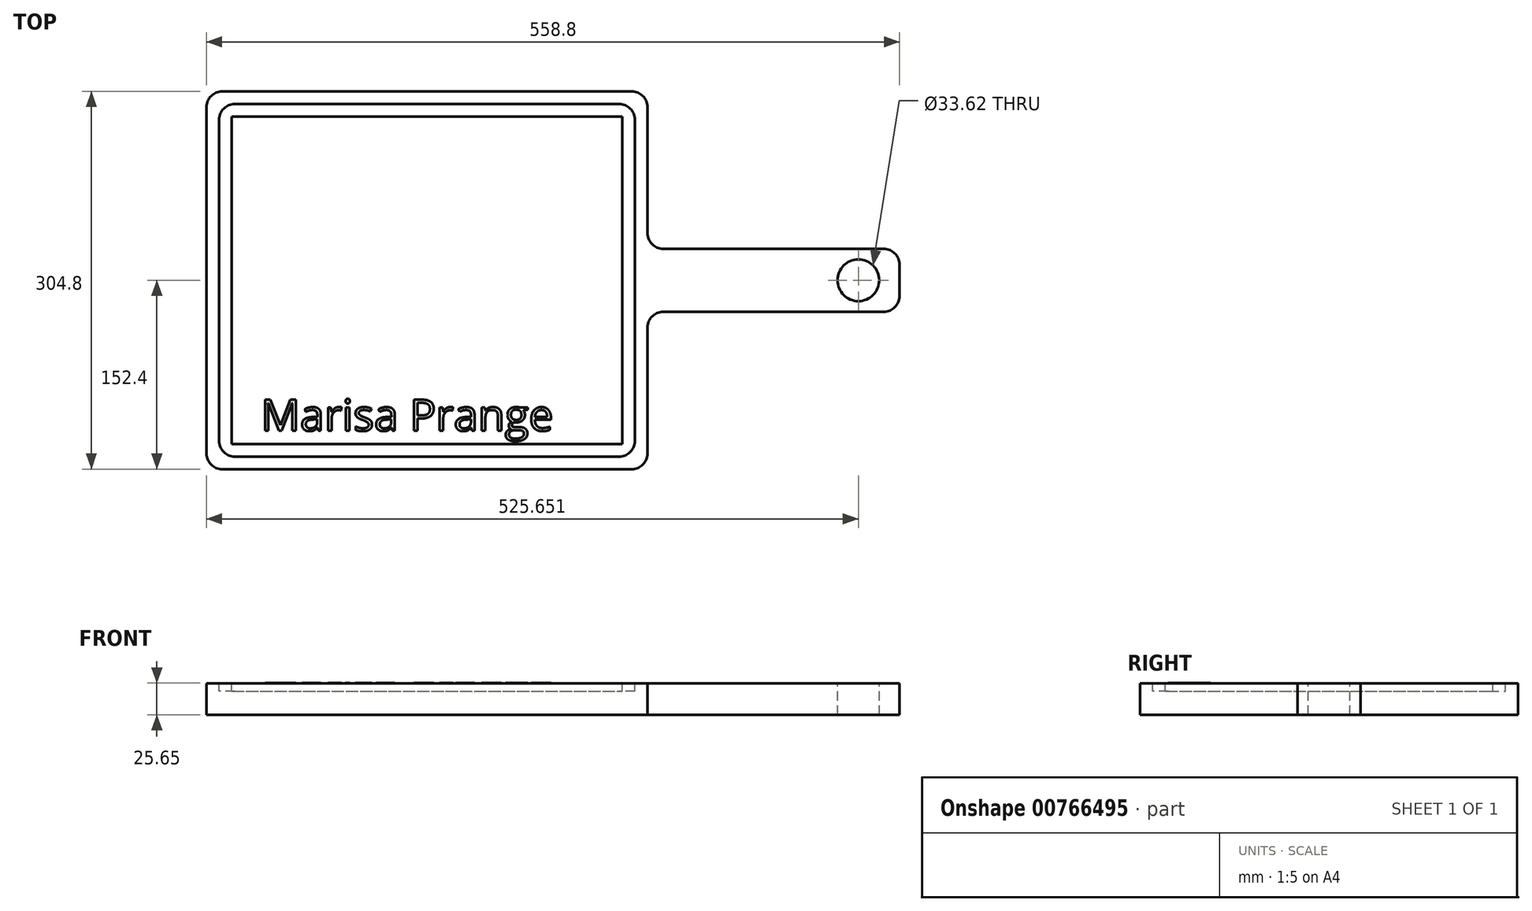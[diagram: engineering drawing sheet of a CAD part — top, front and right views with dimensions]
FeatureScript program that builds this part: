
annotation { "Feature Type Name" : "Feature", "Feature Type Description" : "" }
export const myFeature = defineFeature(function(context is Context, id is Id, definition is map)
    precondition{}
    {
        {
            var Q0;
            Q0=qCreatedBy(makeId("Top.planeOp"),FACE);
            var sketch = newSketch(context, id + "F0", { "sketchPlane" : qUnion([Q0])});
            skLineSegment(sketch, "E0.bottom", {"start": v(0, 0) * mm, "end": v(355.6, 0) * mm});
            skLineSegment(sketch, "E0.top", {"start": v(0, 304.8) * mm, "end": v(355.6, 304.8) * mm});
            skLineSegment(sketch, "E0.left", {"start": v(0, 0) * mm, "end": v(0, 304.8) * mm});
            skLineSegment(sketch, "E0.right", {"start": v(355.6, 0) * mm, "end": v(355.6, 304.8) * mm});
            skLineSegment(sketch, "E1.bottom", {"start": v(355.6, 177.8) * mm, "end": v(558.8, 177.8) * mm});
            skLineSegment(sketch, "E1.top", {"start": v(355.6, 127) * mm, "end": v(558.8, 127) * mm});
            skLineSegment(sketch, "E1.left", {"start": v(355.6, 177.8) * mm, "end": v(355.6, 127) * mm});
            skLineSegment(sketch, "E1.right", {"start": v(558.8, 177.8) * mm, "end": v(558.8, 127) * mm});
            skSolve(sketch);
        }
        {
            var Q0;
            {var subQ1=sQuery(id+"F0.wireOp",EDGE,"E0.bottom");Q0=makeQuery(id+"F0.imprint","IMPRINT",FACE,{"disambiguationData":[TD([[makeQuery(id+"F0.imprint","IMPRINT",EDGE,{"derivedFrom":subQ1}),1.0]])]});}
            var Q1;
            Q1=makeQuery(id+"F0.imprint","IMPRINT",FACE,{"disambiguationData":[TD([[makeQuery(id+"F0.imprint","IMPRINT",EDGE,{"derivedFrom":sQuery(id+"F0.wireOp",EDGE,"E1.bottom")}),-1.0]])]});
            extrude(context, id + "F1", {"entities" : qUnion([Q0, Q1]), "depth" : 25.4 * mm, "offsetDistance" : 25.4 * mm});
        }
        {
            var Q0;
            Q0=makeQuery(id+"F1.opExtrude","CAP_FACE",FACE,{"disambiguationData":[OSD([sQuery(id+"F0.wireOp",EDGE,"E0.bottom"),sQuery(id+"F0.wireOp",EDGE,"E0.top"),sQuery(id+"F0.wireOp",EDGE,"E0.left"),sQuery(id+"F0.wireOp",EDGE,"E0.right"),sQuery(id+"F0.wireOp",EDGE,"E1.bottom"),sQuery(id+"F0.wireOp",EDGE,"E1.top"),sQuery(id+"F0.wireOp",EDGE,"E1.right")])],"isStart":false});
            var sketch = newSketch(context, id + "F2", { "sketchPlane" : qUnion([Q0])});
            skCircle(sketch, "E2", {"center": v(525.65, 152.4) * mm, "radius": 16.81 * mm});
            skPoint(sketch, "E2.centerSnap0", {"position": v(558.8, 152.4) * mm});
            skSolve(sketch);
        }
        {
            var Q0;
            Q0 = qSketchRegion(id + "F2", true);
            extrude(context, id + "F3", {"entities" : qUnion([Q0]), "operationType" : NewBodyOperationType.REMOVE, "oppositeDirection" : true, "depth" : 25.4 * mm, "offsetDistance" : 25.4 * mm});
        }
        {
            var Q0;
            Q0=makeQuery(id+"F1.opExtrude","CAP_FACE",FACE,{"disambiguationData":[OSD([sQuery(id+"F0.wireOp",EDGE,"E0.bottom"),sQuery(id+"F0.wireOp",EDGE,"E0.top"),sQuery(id+"F0.wireOp",EDGE,"E0.left"),sQuery(id+"F0.wireOp",EDGE,"E0.right"),sQuery(id+"F0.wireOp",EDGE,"E1.bottom"),sQuery(id+"F0.wireOp",EDGE,"E1.top"),sQuery(id+"F0.wireOp",EDGE,"E1.right")])],"isStart":false});
            var sketch = newSketch(context, id + "F4", { "sketchPlane" : qUnion([Q0])});
            skLineSegment(sketch, "E3.0", {"start": v(345.44, 177.8) * mm, "end": v(345.44, 294.64) * mm});
            skLineSegment(sketch, "E3.1", {"start": v(345.44, 10.16) * mm, "end": v(345.44, 127) * mm});
            skLineSegment(sketch, "E3.2", {"start": v(10.16, 10.16) * mm, "end": v(345.44, 10.16) * mm});
            skLineSegment(sketch, "E3.3", {"start": v(10.16, 10.16) * mm, "end": v(10.16, 294.64) * mm});
            skLineSegment(sketch, "E3.4", {"start": v(10.16, 294.64) * mm, "end": v(345.44, 294.64) * mm});
            skLineSegment(sketch, "E4", {"start": v(345.44, 177.8) * mm, "end": v(345.44, 127) * mm});
            skLineSegment(sketch, "E5.0", {"start": v(20.32, 20.32) * mm, "end": v(20.32, 284.48) * mm});
            skLineSegment(sketch, "E5.1", {"start": v(335.28, 177.8) * mm, "end": v(335.28, 284.48) * mm});
            skLineSegment(sketch, "E5.2", {"start": v(335.28, 177.8) * mm, "end": v(335.28, 127) * mm});
            skLineSegment(sketch, "E5.3", {"start": v(20.32, 284.48) * mm, "end": v(335.28, 284.48) * mm});
            skLineSegment(sketch, "E5.4", {"start": v(335.28, 20.32) * mm, "end": v(335.28, 127) * mm});
            skLineSegment(sketch, "E5.5", {"start": v(20.32, 20.32) * mm, "end": v(335.28, 20.32) * mm});
            skText(sketch, "E6", { "text": "Marisa ", "fontName": "OpenSans-Regular.ttf"});
            const initialGuessF4  = {"E6": [0.02032, 0.0225, 1, 0, 0.0261]};
            skSetInitialGuess(sketch, initialGuessF4);
            skSolve(sketch);
        }
        {
            var Q0;
            Q0=makeQuery(id+"F4.imprint","IMPRINT",FACE,{"disambiguationData":[TD([[makeQuery(id+"F4.imprint","IMPRINT",EDGE,{"derivedFrom":sQuery(id+"F4.wireOp",EDGE,"E3.0")}),1.0]])]});
            extrude(context, id + "F5", {"entities" : qUnion([Q0]), "operationType" : NewBodyOperationType.REMOVE, "oppositeDirection" : true, "depth" : 6.35 * mm, "offsetDistance" : 25.4 * mm});
        }
        {
            var Q0;
            Q0=makeQuery(id+"F5.boolean.opBoolean","COPY",EDGE,{"derivedFrom":makeQuery(id+"F5.opExtrude","SWEPT_EDGE",EDGE,{"disambiguationData":[OSD([sQuery(id+"F4.wireOp",EDGE,"E3.3"),sQuery(id+"F4.wireOp",EDGE,"E3.4")])]})});
            var Q1;
            Q1=makeQuery(id+"F5.boolean.opBoolean","COPY",EDGE,{"derivedFrom":makeQuery(id+"F5.opExtrude","SWEPT_EDGE",EDGE,{"disambiguationData":[OSD([sQuery(id+"F4.wireOp",EDGE,"E3.2"),sQuery(id+"F4.wireOp",EDGE,"E3.3")])]})});
            var Q2;
            Q2=makeQuery(id+"F5.boolean.opBoolean","COPY",EDGE,{"derivedFrom":makeQuery(id+"F5.opExtrude","SWEPT_EDGE",EDGE,{"disambiguationData":[OSD([sQuery(id+"F4.wireOp",EDGE,"E3.1"),sQuery(id+"F4.wireOp",EDGE,"E3.2")])]})});
            var Q3;
            Q3=makeQuery(id+"F5.boolean.opBoolean","COPY",EDGE,{"derivedFrom":makeQuery(id+"F5.opExtrude","SWEPT_EDGE",EDGE,{"disambiguationData":[OSD([sQuery(id+"F4.wireOp",EDGE,"E3.0"),sQuery(id+"F4.wireOp",EDGE,"E3.4")])]})});
            var Q4;
            Q4=makeQuery(id+"F1.opExtrude","SWEPT_EDGE",EDGE,{"disambiguationData":[OSD([sQuery(id+"F0.wireOp",EDGE,"E0.top"),sQuery(id+"F0.wireOp",EDGE,"E0.right")])]});
            var Q5;
            Q5=makeQuery(id+"F1.opExtrude","SWEPT_EDGE",EDGE,{"disambiguationData":[OSD([sQuery(id+"F0.wireOp",EDGE,"E0.top"),sQuery(id+"F0.wireOp",EDGE,"E0.left")])]});
            var Q6;
            Q6=makeQuery(id+"F1.opExtrude","SWEPT_EDGE",EDGE,{"disambiguationData":[OSD([sQuery(id+"F0.wireOp",EDGE,"E0.bottom"),sQuery(id+"F0.wireOp",EDGE,"E0.left")])]});
            var Q7;
            Q7=makeQuery(id+"F1.opExtrude","SWEPT_EDGE",EDGE,{"disambiguationData":[OSD([sQuery(id+"F0.wireOp",EDGE,"E0.bottom"),sQuery(id+"F0.wireOp",EDGE,"E0.right")])]});
            var Q8;
            Q8=makeQuery(id+"F1.opExtrude","SWEPT_EDGE",EDGE,{"disambiguationData":[OSD([sQuery(id+"F0.wireOp",EDGE,"E1.top"),sQuery(id+"F0.wireOp",EDGE,"E1.right")])]});
            var Q9;
            Q9=makeQuery(id+"F1.opExtrude","SWEPT_EDGE",EDGE,{"disambiguationData":[OSD([sQuery(id+"F0.wireOp",EDGE,"E1.bottom"),sQuery(id+"F0.wireOp",EDGE,"E1.right")])]});
            var Q10;
            Q10=makeQuery(id+"F1.opExtrude","SWEPT_EDGE",EDGE,{"disambiguationData":[OSD([sQuery(id+"F0.wireOp",EDGE,"E0.right"),sQuery(id+"F0.wireOp",EDGE,"E1.top"),sQuery(id+"F0.wireOp",EDGE,"E1.left")])]});
            var Q11;
            Q11=makeQuery(id+"F1.opExtrude","SWEPT_EDGE",EDGE,{"disambiguationData":[OSD([sQuery(id+"F0.wireOp",EDGE,"E0.right"),sQuery(id+"F0.wireOp",EDGE,"E1.bottom"),sQuery(id+"F0.wireOp",EDGE,"E1.left")])]});
            fillet(context, id + "F6", {"entities" : qUnion([Q0, Q1, Q2, Q3, Q4, Q5, Q6, Q7, Q8, Q9, Q10, Q11]), "radius" : 12.7 * mm, "tangentPropagation" : true, "allowEdgeOverflow" : false});
        }
        {
            var Q0;
            Q0=makeQuery(id+"F5.boolean.opBoolean","SPLIT",FACE,{"disambiguationData":[TD([makeQuery(id+"F5.opExtrude","SWEPT_FACE",FACE,{"disambiguationData":[OSD([sQuery(id+"F4.wireOp",EDGE,"E5.0")])]})])],"derivedFrom":makeQuery(id+"F1.opExtrude","CAP_FACE",FACE,{"disambiguationData":[OSD([sQuery(id+"F0.wireOp",EDGE,"E0.bottom"),sQuery(id+"F0.wireOp",EDGE,"E0.top"),sQuery(id+"F0.wireOp",EDGE,"E0.left"),sQuery(id+"F0.wireOp",EDGE,"E0.right"),sQuery(id+"F0.wireOp",EDGE,"E1.bottom"),sQuery(id+"F0.wireOp",EDGE,"E1.top"),sQuery(id+"F0.wireOp",EDGE,"E1.right")])],"isStart":false})});
            var sketch = newSketch(context, id + "F7", { "sketchPlane" : qUnion([Q0])});
            skText(sketch, "E7", { "text": "Marisa Prange ", "fontName": "OpenSans-Regular.ttf"});
            const initialGuessF7  = {"E7": [0.04371, 0.03097, 1, 0, 0.02534]};
            skSetInitialGuess(sketch, initialGuessF7);
            skSolve(sketch);
        }
        {
            var Q0;
            Q0 = qSketchRegion(id + "F7", true);
            extrude(context, id + "F8", {"entities" : qUnion([Q0]), "operationType" : NewBodyOperationType.ADD, "depth" : 0.25 * mm, "offsetDistance" : 25.4 * mm});
        }
    });
